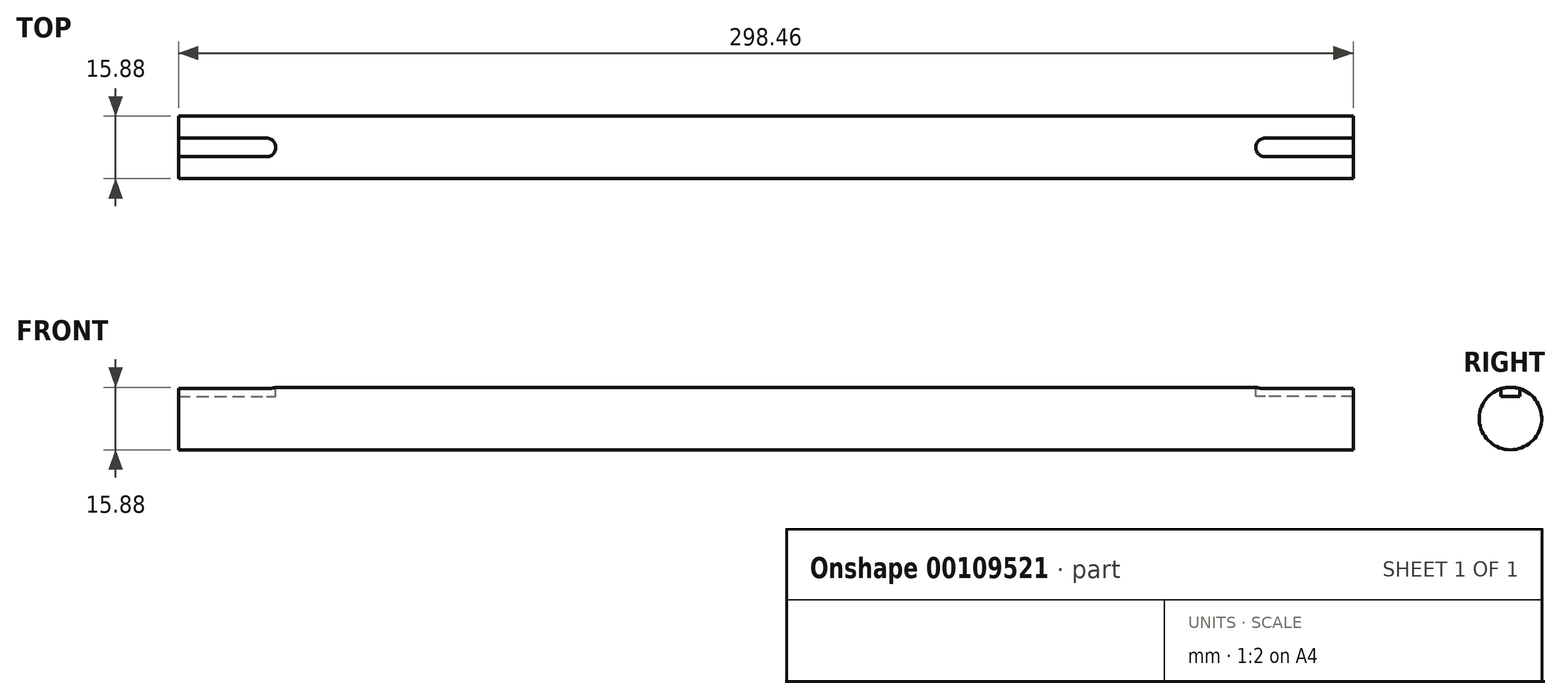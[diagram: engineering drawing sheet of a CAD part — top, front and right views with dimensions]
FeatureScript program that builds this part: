
annotation { "Feature Type Name" : "Feature", "Feature Type Description" : "" }
export const myFeature = defineFeature(function(context is Context, id is Id, definition is map)
    precondition{}
    {
        {
            var Q0;
            Q0=qCreatedBy(makeId("Right.planeOp"),FACE);
            var sketch = newSketch(context, id + "F0", { "sketchPlane" : qUnion([Q0])});
            skCircle(sketch, "E0", {"center": v(0, 0) * mm, "radius": 7.94 * mm});
            skSolve(sketch);
        }
        {
            var Q0;
            Q0=qSketchRegion(id+"F0",true);
            extrude(context, id + "F1", {"entities" : qUnion([Q0]), "endBound" : BoundingType.SYMMETRIC, "depth" : 298.45 * mm});
        }
        {
            var Q0;
            Q0=qCreatedBy(makeId("Top.planeOp"),FACE);
            cPlane(context, id + "F2", {"entities" : qUnion([Q0]), "cplaneType" : CPlaneType.OFFSET, "offset" : 7.94 * mm, "width" : 152.4 * mm, "height" : 152.4 * mm});
        }
        {
            var Q0;
            Q0=qCreatedBy(id+"F2.planeOp",FACE);
            var sketch = newSketch(context, id + "F3", { "sketchPlane" : qUnion([Q0])});
            skLineSegment(sketch, "E1", {"start": v(119.36, 0) * mm, "end": v(-3.63, 0) * mm, "construction": true});
            skLineSegment(sketch, "E2.0", {"start": v(149.23, 7.94) * mm, "end": v(149.23, -7.94) * mm, "construction": true});
            skLineSegment(sketch, "E3", {"start": v(149.23, 0) * mm, "end": v(126.87, 0) * mm});
            skArc(sketch, "E4.0.startCap", {"start": v(149.23, 2.38) * mm, "mid": v(151.6, 0) * mm, "end": v(149.23, -2.38) * mm});
            skArc(sketch, "E4.0.endCap", {"start": v(126.87, -2.38) * mm, "mid": v(124.5, 0) * mm, "end": v(126.87, 2.38) * mm});
            skLineSegment(sketch, "E4.0.left", {"start": v(149.23, -2.38) * mm, "end": v(126.87, -2.38) * mm});
            skLineSegment(sketch, "E4.0.right", {"start": v(149.23, 2.38) * mm, "end": v(126.87, 2.38) * mm});
            skArc(sketch, "E5.MirrorCS", {"start": v(-126.87, -2.38) * mm, "mid": v(-124.5, 0) * mm, "end": v(-126.87, 2.38) * mm});
            skArc(sketch, "E6.MirrorCS", {"start": v(-149.23, 2.38) * mm, "mid": v(-151.6, 0) * mm, "end": v(-149.23, -2.38) * mm});
            skLineSegment(sketch, "E7.MirrorCS", {"start": v(-149.23, 7.94) * mm, "end": v(-149.23, -7.94) * mm});
            skLineSegment(sketch, "E8.MirrorCS", {"start": v(-149.23, 2.38) * mm, "end": v(-126.87, 2.38) * mm});
            skLineSegment(sketch, "E9.MirrorCS", {"start": v(-149.23, -2.38) * mm, "end": v(-126.87, -2.38) * mm});
            skLineSegment(sketch, "E10.MirrorCS", {"start": v(-149.23, 0) * mm, "end": v(-126.87, 0) * mm});
            skSolve(sketch);
        }
        {
            var Q0;
            Q0=qSketchRegion(id+"F3",true);
            extrude(context, id + "F4", {"entities" : qUnion([Q0]), "operationType" : NewBodyOperationType.REMOVE, "oppositeDirection" : true, "depth" : 2.38 * mm});
        }
    });
